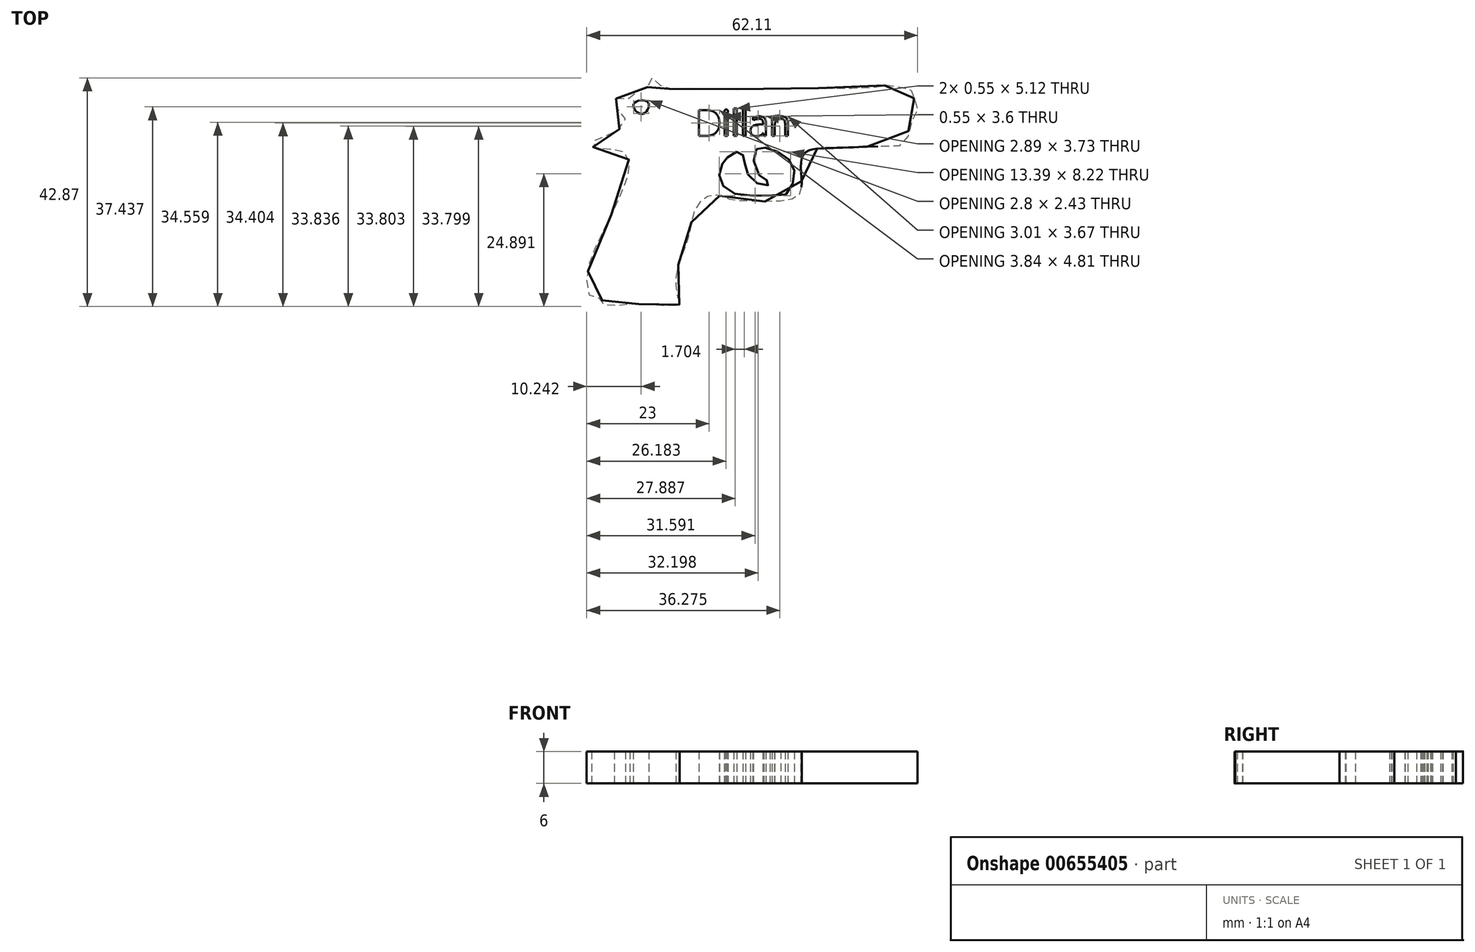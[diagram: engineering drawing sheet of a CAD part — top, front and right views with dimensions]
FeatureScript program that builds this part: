
annotation { "Feature Type Name" : "Feature", "Feature Type Description" : "" }
export const myFeature = defineFeature(function(context is Context, id is Id, definition is map)
    precondition{}
    {
        {
            var Q0;
            Q0=qCreatedBy(makeId("Top.planeOp"),FACE);
            var sketch = newSketch(context, id + "F0", { "sketchPlane" : qUnion([Q0])});
            skFitSpline(sketch, "E0", {"points": [v(-60.55, 59.19) * mm, v(-58.16, 59.24) * mm, v(-57.16, 60.24) * mm, v(-54.83, 61.08) * mm, v(-54.21, 62.74) * mm, v(-53.16, 62.9) * mm, v(-51.94, 61.24) * mm, v(-49.71, 61.13) * mm, v(-42.32, 60.96) * mm, v(-30.98, 61.13) * mm, v(-19.48, 61.13) * mm, v(-11.2, 61.4) * mm, v(-9.36, 61.69) * mm, v(-5.97, 61.08) * mm, v(-5.25, 60.85) * mm, v(-4.53, 58.96) * mm, v(-4.08, 57.85) * mm, v(-4.08, 56.63) * mm, v(-5.58, 53.68) * mm, v(-6.25, 50.8) * mm, v(-11.8, 50.18) * mm, v(-15.53, 50.07) * mm, v(-20.59, 49.9) * mm, v(-24.04, 49.57) * mm, v(-25.54, 48.4) * mm, v(-25.81, 44.85) * mm, v(-25.98, 41.51) * mm, v(-28.2, 40.12) * mm, v(-35.54, 39.96) * mm, v(-39.15, 40.23) * mm, v(-40.65, 40.85) * mm, v(-43.27, 40.85) * mm, v(-45.66, 38.51) * mm, v(-46.54, 35.18) * mm, v(-47.27, 32.29) * mm, v(-48.66, 28.67) * mm, v(-49.32, 25.5) * mm, v(-48.99, 21.84) * mm, v(-48.66, 20.56) * mm, v(-50.71, 20.34) * mm, v(-53.77, 20.4) * mm, v(-56.83, 20.67) * mm, v(-59.5, 20.45) * mm, v(-62.77, 20.45) * mm, v(-63.33, 21.56) * mm, v(-64.27, 21.67) * mm, v(-65.83, 22.73) * mm, v(-65.72, 27.28) * mm, v(-64.89, 30.17) * mm, v(-60.44, 39.46) * mm, v(-58.05, 45.8) * mm, v(-58.27, 48.07) * mm, v(-59.83, 49.57) * mm, v(-63.5, 49.63) * mm, v(-65.1, 50.46) * mm, v(-64.16, 51.63) * mm, v(-62.38, 52.18) * mm, v(-59.55, 53.8) * mm, v(-58.88, 55.74) * mm, v(-60.66, 57.74) * mm, v(-60.55, 59.19) * mm]});
            skFitSpline(sketch, "E1", {"points": [v(-37.93, 49.18) * mm, v(-39.65, 48.13) * mm, v(-40.38, 47.35) * mm, v(-41.15, 45.4) * mm, v(-40.7, 43.18) * mm, v(-38.1, 41.23) * mm, v(-31.82, 41.01) * mm, v(-28.54, 41.3) * mm, v(-27.26, 43.9) * mm, v(-27.37, 46.63) * mm, v(-29.48, 48.85) * mm, v(-32.37, 49.9) * mm, v(-33.93, 49.9) * mm, v(-34.76, 48.07) * mm, v(-33.48, 44.57) * mm, v(-32.37, 43.9) * mm, v(-31.7, 43.12) * mm, v(-32.82, 42.9) * mm, v(-35.15, 44.07) * mm, v(-36.32, 46.3) * mm, v(-36.48, 47.68) * mm, v(-37.04, 49.02) * mm, v(-37.93, 49.18) * mm]});
            skFitSpline(sketch, "E2", {"points": [v(-57.24, 58.12) * mm, v(-55.64, 56.29) * mm, v(-54.54, 58.48) * mm, v(-57.24, 58.12) * mm]});
            skText(sketch, "E3", { "text": "Dillan", "fontName": "OpenSans-Regular.ttf"});
            const initialGuessF0  = {"E3": [-0.04566, 0.05218, 1, 0, 0.00485]};
            skSetInitialGuess(sketch, initialGuessF0);
            skSolve(sketch);
        }
        {
            var Q0;
            Q0 = qSketchRegion(id + "F0", true);
            extrude(context, id + "F1", {"entities" : qUnion([Q0]), "depth" : 6 * mm, "offsetDistance" : 25.4 * mm});
        }
    });
